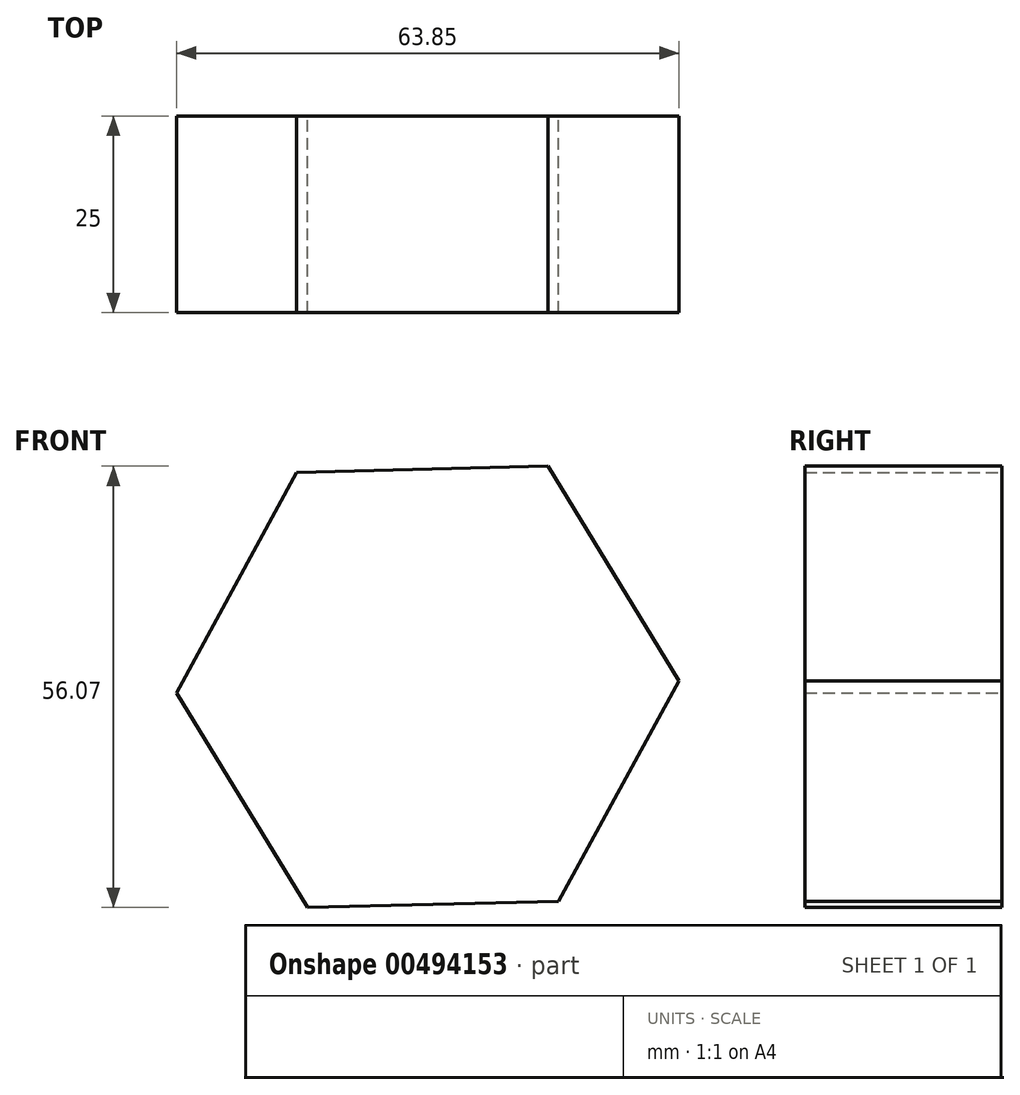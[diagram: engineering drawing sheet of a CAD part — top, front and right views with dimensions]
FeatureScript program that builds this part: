
annotation { "Feature Type Name" : "Feature", "Feature Type Description" : "" }
export const myFeature = defineFeature(function(context is Context, id is Id, definition is map)
    precondition{}
    {
        {
            var Q0;
            Q0=qCreatedBy(makeId("Front.planeOp"),FACE);
            var sketch = newSketch(context, id + "F0", { "sketchPlane" : qUnion([Q0])});
            skCircle(sketch, "E0.cCircle", {"center": v(-6.02, 9.9) * mm, "radius": 31.93 * mm, "construction": true});
            skLineSegment(sketch, "E0.0", {"start": v(10.61, -17.36) * mm, "end": v(-21.3, -18.14) * mm});
            skLineSegment(sketch, "E0.1", {"start": v(-21.3, -18.14) * mm, "end": v(-37.95, 9.11) * mm});
            skLineSegment(sketch, "E0.2", {"start": v(-37.95, 9.11) * mm, "end": v(-22.66, 37.15) * mm});
            skLineSegment(sketch, "E0.3", {"start": v(-22.66, 37.15) * mm, "end": v(9.26, 37.93) * mm});
            skLineSegment(sketch, "E0.4", {"start": v(9.26, 37.93) * mm, "end": v(25.9, 10.68) * mm});
            skLineSegment(sketch, "E0.5", {"start": v(25.9, 10.68) * mm, "end": v(10.61, -17.36) * mm});
            skSolve(sketch);
        }
        {
            var Q0;
            Q0=makeQuery(id+"F0.imprint","IMPRINT",FACE,{"disambiguationData":[TD([[makeQuery(id+"F0.imprint","IMPRINT",EDGE,{"derivedFrom":sQuery(id+"F0.wireOp",EDGE,"E0.0")}),-1.0]])]});
            extrude(context, id + "F1", {"entities" : qUnion([Q0]), "depth" : 25 * mm});
        }
    });
